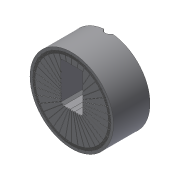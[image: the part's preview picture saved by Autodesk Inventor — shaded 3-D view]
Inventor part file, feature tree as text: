
AUTODESK INVENTOR PART (.ipt)
format: ipt  version: 2018 (Build 220112000, 112)  size: 2,192,384 bytes
history: native  units: mm
features: sketch x29, extrude x25, projected_geometry x23, fillet x7, hole x4, chamfer x3, pattern_circular x2, mirror x1
ambient origin geometry x8: Origin, YZ Plane, XZ Plane, XY Plane, X Axis, Y Axis, Z Axis, Center Point
bodies: Solid1 (feature_tree)
feature tree (94):
  extrude  "Extrusion1"  Depth=45.0mm
  extrude  "Extrusion2"  Depth=2.25mm
  hole  "Hole1"  [1 undecoded]
  hole  "Hole2"  [1 undecoded]
  fillet  "Fillet1"  Radius=14.0mm
  extrude  "Extrusion3"  Depth=18.5mm
  extrude  "Extrusion4"  Depth=10.0mm
  extrude  "Extrusion5"  Depth=2.195mm
  extrude  "Extrusion6"  Depth=20.5mm
  hole  "Hole3"  [1 undecoded]
  extrude  "Extrusion7"  Depth=0.5mm
  extrude  "Extrusion8"  Depth=5.0mm TaperAngle=0.0deg
  extrude  "Extrusion9"  Depth=10.0mm
  extrude  "Extrusion10"  Depth=10.0mm
  extrude  "Extrusion11"  Depth=14.5mm
  extrude  "Extrusion12"  Depth=14.5mm
  extrude  "Extrusion13"  Depth=5.0mm
  extrude  "Extrusion14"  Depth=2.25mm
  extrude  "Extrusion15"  Depth=2.25mm
  extrude  "Extrusion16"  Depth=9.0mm
  extrude  "Extrusion17"  Depth=1.0mm
  chamfer  "Chamfer1"  Distance=1.0mm
  fillet  "Fillet7"  Radius=20.7mm
  fillet  "Fillet8"  Radius=32.0mm
  mirror  "Mirror1"
  extrude  "Extrusion18"  Depth=1.0mm TaperAngle=0.0deg
  hole  "Hole5"  [1 undecoded]
  extrude  "Extrusion19"  Depth=0.2mm TaperAngle=0.0deg
  extrude  "Extrusion20"  Depth=0.5mm TaperAngle=0.0deg
  extrude  "Extrusion21"  Depth=5.0mm TaperAngle=0.0deg
  fillet  "Fillet9"  Radius=5.0mm
  extrude  "Extrusion22"  Depth=1.0mm TaperAngle=0.0deg
  chamfer  "Chamfer2"  Distance=2.5mm Angle=45.0deg
  chamfer  "Chamfer3"  Distance=1.5mm
  fillet  "Fillet10"  Radius=0.5mm
  extrude  "Extrusion26"  Depth=1.0mm TaperAngle=0.0deg
  fillet  "Fillet12"  Radius=5.0mm
  pattern_circular  "Circular Pattern4"  [2 undecoded]
  extrude  "Extrusion23"  Depth=1.0mm
  fillet  "Fillet11"  Radius=13.0mm
  pattern_circular  "Circular Pattern2"  [2 undecoded]
  extrude  "Extrusion27"  Depth=1.0mm
  sketch  "Sketch1"  dims[d0=24.5mm d1=45.0mm]
  sketch  "Sketch2"  dims[d2=1.95mm d3=0.0mm d4=2.25mm]
  projected_geometry  "Projected Loop1"
  sketch  "Sketch3"  dims[d5=20.0mm d6=2.25mm]
  projected_geometry  "Projected Loop2"
  sketch  "Sketch4"  dims[d7=5.25mm d8=5.25mm d9=14.0mm]
  projected_geometry  "Projected Loop3"
  sketch  "Sketch5"  dims[d10=5.25mm d11=18.5mm]
  projected_geometry  "Projected Loop4"
  sketch  "Sketch6"  dims[d12=10.0mm d13=0.0mm d14=20.5mm]
  projected_geometry  "Projected Loop5"
  sketch  "Sketch7"  dims[d15=2.0mm d16=2.195mm]
  projected_geometry  "Projected Loop6"
  sketch  "Sketch8"  dims[d17=2.0mm]
  projected_geometry  "Projected Loop7"
  sketch  "Sketch9"  dims[d18=2.4mm d19=6.0mm d20=4.4mm d21=2.0mm d22=90.0deg d23=8.0mm d24=20.594885mm d25=20.5mm]
  projected_geometry  "Projected Loop8"
  projected_geometry  "Projected Loop9"
  sketch  "Sketch10"  dims[d26=26.65mm d27=2.0mm]
  projected_geometry  "Projected Loop10"
  projected_geometry  "Projected Loop11"
  sketch  "Sketch11"  dims[d28=2.0mm]
  projected_geometry  "Projected Loop12"
  sketch  "Sketch12"  dims[d29=2.4mm d30=6.0mm d31=4.4mm d32=2.0mm d33=90.0deg d34=8.0mm d35=20.594885mm d36=0.5mm]
  sketch  "Sketch13"  dims[d37=18.0mm d38=5.0mm d39=0.0mm]
  sketch  "Sketch14"  dims[d41=10.0mm d42=0.0mm d43=24.5mm]
  projected_geometry  "Projected Loop13"
  sketch  "Sketch15"  dims[d44=1.15mm d45=0.0mm d46=10.0mm]
  sketch  "Sketch16"  dims[d47=21.0mm d48=14.5mm]
  projected_geometry  "Projected Loop14"
  sketch  "Sketch17"  dims[d49=20.0mm d50=14.5mm]
  projected_geometry  "Projected Loop15"
  sketch  "Sketch18"  dims[d51=24.5mm d52=5.0mm]
  projected_geometry  "Projected Loop16"
  sketch  "Sketch19"  dims[d53=5.0mm d54=2.25mm]
  projected_geometry  "Projected Loop17"
  sketch  "Sketch20"  dims[d55=2.25mm d56=5.0mm]
  projected_geometry  "Projected Loop18"
  sketch  "Sketch22"  dims[d57=5.0mm d58=9.0mm]
  sketch  "Sketch24"  dims[d59=14.75mm d60=4.0mm d61=1.0mm d62=0.0mm d63=20.7mm]
  projected_geometry  "Projected Loop21"
  sketch  "Sketch25"  dims[d64=2.4mm d65=6.0mm d66=4.4mm d67=2.0mm d68=90.0deg d69=8.0mm d70=20.594885mm d72=32.0mm]
  projected_geometry  "Projected Loop22"
  sketch  "Sketch26"  dims[d73=5.0mm d74=0.0mm d75=1.0mm d76=0.0mm]
  projected_geometry  "Projected Loop23"
  sketch  "Sketch27"  dims[d77=12.25mm d78=0.0mm d80=8.0mm]
  projected_geometry  "Projected Loop24"
  sketch  "Sketch28"  dims[d81=4.5mm d82=0.0mm d84=0.2mm d85=0.0mm]
  projected_geometry  "Projected Loop25"
  sketch  "Sketch29"  dims[d86=21.0mm d87=0.5mm d88=0.0mm]
  sketch  "Sketch33"  dims[d91=8.0mm d92=0.0mm d93=5.0mm d94=0.0mm d95=5.0mm d96=0.0mm]
  sketch  "Sketch34"  dims[d98=0.2mm d99=0.0mm d100=0.2mm d101=0.0mm d102=2.5mm d103=2.0mm d104=45.0deg d105=1.5mm d114=0.5mm d115=22.55mm d116=0.0mm d117=5.0mm d118=5.0mm d119=13.0mm d120=13.0mm d121=3.2mm d122=6.0mm d123=6.3mm d124=2.0mm d125=90.0deg d126=8.0mm d127=20.594885mm d128=19.0mm d129=0.0mm d130=95.0mm d131=20.0mm d132=0.0mm d133=4.5mm d134=4.5mm d135=4.5mm d136=4.5mm d137=2.0mm d138=0.0mm d139=0.8mm d140=10.0mm d141=36.0mm d142=3.5mm d143=0.0mm d144=5.0mm d145=2.0mm d146=45.0deg d147=3.0mm d148=2.0mm d149=45.0deg d150=3.0mm d151=0.5mm d152=90.0mm d153=1.0mm d154=0.0mm d158=0.25mm d159=190.0mm d160=180.0deg d174=0.3mm d175=3.0mm d176=43.0mm d177=0.5mm d178=0.0mm d179=0.15mm d180=3600.0mm d181=360.0deg d183=2.0mm d184=0.0mm d162=1.0mm d163=1.0mm]
note: 8 required parameter values undecoded (feature->parameter linkage not recoverable at this tier; creation-order binding heuristic only, values carry confidence <= 0.55)
